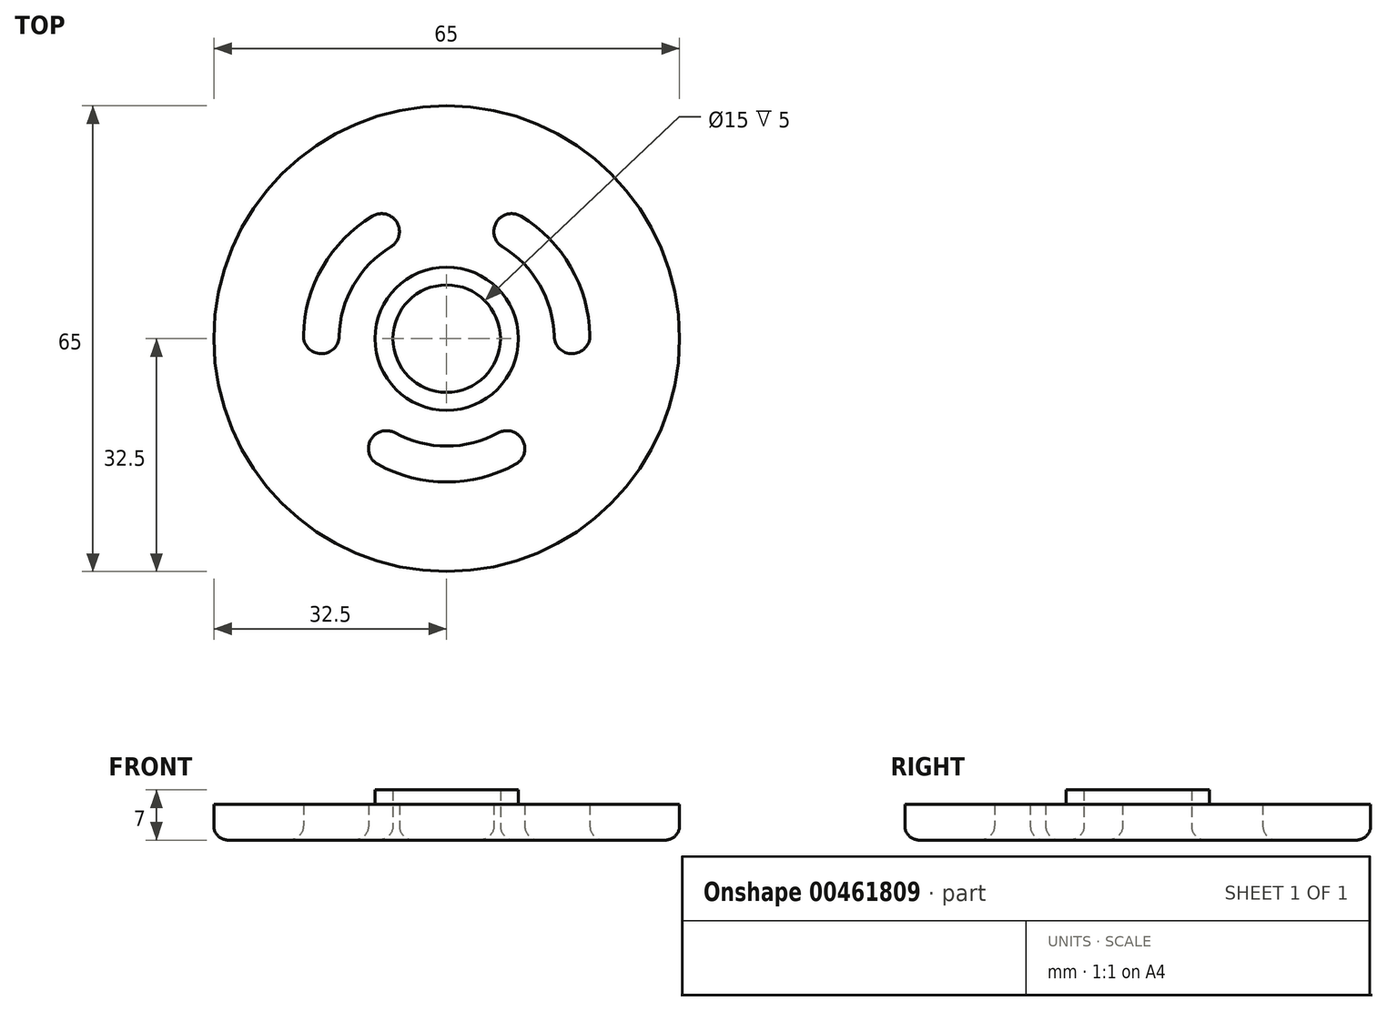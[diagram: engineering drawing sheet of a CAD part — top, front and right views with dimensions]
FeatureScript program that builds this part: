
annotation { "Feature Type Name" : "Feature", "Feature Type Description" : "" }
export const myFeature = defineFeature(function(context is Context, id is Id, definition is map)
    precondition{}
    {
        {
            var Q0;
            Q0=qCreatedBy(makeId("Top.planeOp"),FACE);
            var sketch = newSketch(context, id + "F0", { "sketchPlane" : qUnion([Q0])});
            skCircle(sketch, "E0", {"center": v(0, 0) * mm, "radius": 32.5 * mm});
            skCircle(sketch, "E1", {"center": v(0, 0) * mm, "radius": 10 * mm});
            skLineSegment(sketch, "E2", {"start": v(-10, 0) * mm, "end": v(-15, 0) * mm, "construction": true});
            skCircle(sketch, "E3", {"center": v(0, 0) * mm, "radius": 15 * mm, "construction": true});
            skPoint(sketch, "E4", {"position": v(0, 15) * mm});
            skPoint(sketch, "E5", {"position": v(13, -7.5) * mm});
            skPoint(sketch, "E6", {"position": v(-13, -7.5) * mm});
            skLineSegment(sketch, "E7", {"start": v(0, 0) * mm, "end": v(13, -7.5) * mm});
            skLineSegment(sketch, "E8", {"start": v(0, 15) * mm, "end": v(0, 0) * mm});
            skLineSegment(sketch, "E9", {"start": v(-13, -7.5) * mm, "end": v(0, 0) * mm});
            skLineSegment(sketch, "E10", {"start": v(-9.01, -12) * mm, "end": v(0, 0) * mm, "construction": true});
            skLineSegment(sketch, "E11", {"start": v(0, 0) * mm, "end": v(-14.9, -1.8) * mm, "construction": true});
            skCircle(sketch, "E12", {"center": v(0, 0) * mm, "radius": 20 * mm, "construction": true});
            skLineSegment(sketch, "E13", {"start": v(-17.2, -2.09) * mm, "end": v(-17.2, -2.09) * mm});
            skLineSegment(sketch, "E14", {"start": v(-9.01, -12) * mm, "end": v(-12.02, -15.99) * mm, "construction": true});
            skLineSegment(sketch, "E15", {"start": v(-13, -7.5) * mm, "end": v(-17.32, -10) * mm, "construction": true});
            skLineSegment(sketch, "E16.1.0", {"start": v(14.9, -1.8) * mm, "end": v(19.85, -2.41) * mm, "construction": true});
            skLineSegment(sketch, "E16.1.1", {"start": v(9.01, -12) * mm, "end": v(12.02, -15.99) * mm, "construction": true});
            skLineSegment(sketch, "E16.2.0", {"start": v(-6.79, 15.93) * mm, "end": v(-6.79, 15.93) * mm});
            skLineSegment(sketch, "E16.2.1", {"start": v(5.88, 13.8) * mm, "end": v(7.84, 18.4) * mm, "construction": true});
            skArc(sketch, "E17", {"start": v(-10.39, 17.1) * mm, "mid": v(-17.32, 10) * mm, "end": v(-20, 0.45) * mm});
            skArc(sketch, "E18", {"start": v(-7.79, 12.82) * mm, "mid": v(-13, 7.5) * mm, "end": v(-15, 0.34) * mm});
            skPoint(sketch, "E19.visualSharp", {"position": v(-14.9, -1.8) * mm});
            skArc(sketch, "E19.filletArc", {"start": v(-17.2, -2.09) * mm, "mid": v(-15.64, -1.29) * mm, "end": v(-15, 0.34) * mm});
            skPoint(sketch, "E20.visualSharp", {"position": v(-19.85, -2.41) * mm});
            skArc(sketch, "E20.filletArc", {"start": v(-20, 0.45) * mm, "mid": v(-19.17, -1.46) * mm, "end": v(-17.2, -2.09) * mm});
            skPoint(sketch, "E21.visualSharp", {"position": v(-7.84, 18.4) * mm});
            skArc(sketch, "E21.filletArc", {"start": v(-6.79, 15.93) * mm, "mid": v(-8.32, 17.34) * mm, "end": v(-10.39, 17.1) * mm});
            skPoint(sketch, "E22.visualSharp", {"position": v(-5.88, 13.8) * mm});
            skArc(sketch, "E22.filletArc", {"start": v(-7.79, 12.82) * mm, "mid": v(-6.7, 14.2) * mm, "end": v(-6.79, 15.93) * mm});
            skArc(sketch, "E23.1.0", {"start": v(-10.4, -13.85) * mm, "mid": v(-10.85, -15.88) * mm, "end": v(-9.6, -17.54) * mm});
            skArc(sketch, "E23.1.1", {"start": v(10.4, -13.85) * mm, "mid": v(8.93, -12.9) * mm, "end": v(7.2, -13.16) * mm});
            skArc(sketch, "E23.1.2", {"start": v(-7.2, -13.16) * mm, "mid": v(-8.93, -12.9) * mm, "end": v(-10.4, -13.85) * mm});
            skArc(sketch, "E23.1.3", {"start": v(9.6, -17.54) * mm, "mid": v(10.85, -15.88) * mm, "end": v(10.4, -13.85) * mm});
            skArc(sketch, "E23.2.0", {"start": v(17.2, -2.09) * mm, "mid": v(19.17, -1.46) * mm, "end": v(20, 0.45) * mm});
            skArc(sketch, "E23.2.1", {"start": v(6.79, 15.93) * mm, "mid": v(6.7, 14.2) * mm, "end": v(7.79, 12.82) * mm});
            skArc(sketch, "E23.2.2", {"start": v(15, 0.34) * mm, "mid": v(15.64, -1.29) * mm, "end": v(17.2, -2.09) * mm});
            skArc(sketch, "E23.2.3", {"start": v(10.39, 17.1) * mm, "mid": v(8.32, 17.34) * mm, "end": v(6.79, 15.93) * mm});
            skArc(sketch, "E24.1.0", {"start": v(-7.2, -13.16) * mm, "mid": v(0, -15) * mm, "end": v(7.2, -13.16) * mm});
            skArc(sketch, "E24.2.0", {"start": v(15, 0.34) * mm, "mid": v(13, 7.5) * mm, "end": v(7.79, 12.82) * mm});
            skArc(sketch, "E25.1.0", {"start": v(-9.6, -17.54) * mm, "mid": v(0, -20) * mm, "end": v(9.6, -17.54) * mm});
            skArc(sketch, "E25.2.0", {"start": v(20, 0.45) * mm, "mid": v(17.32, 10) * mm, "end": v(10.39, 17.1) * mm});
            skSolve(sketch);
        }
        {
            var Q0;
            Q0=makeQuery(id+"F0.imprint","IMPRINT",FACE,{"disambiguationData":[TD([[makeQuery(id+"F0.imprint","IMPRINT",EDGE,{"derivedFrom":sQuery(id+"F0.wireOp",EDGE,"E0")}),1.0]])]});
            extrude(context, id + "F1", {"entities" : qUnion([Q0]), "depth" : 5 * mm});
        }
        {
            var Q0;
            Q0=makeQuery(id+"F1.opExtrude","CAP_FACE",FACE,{"disambiguationData":[OSD([sQuery(id+"F0.wireOp",EDGE,"E0"),sQuery(id+"F0.wireOp",EDGE,"E1"),sQuery(id+"F0.wireOp",EDGE,"E17"),sQuery(id+"F0.wireOp",EDGE,"E18"),sQuery(id+"F0.wireOp",EDGE,"E19.filletArc"),sQuery(id+"F0.wireOp",EDGE,"E20.filletArc"),sQuery(id+"F0.wireOp",EDGE,"E21.filletArc"),sQuery(id+"F0.wireOp",EDGE,"E22.filletArc"),sQuery(id+"F0.wireOp",EDGE,"E23.1.0"),sQuery(id+"F0.wireOp",EDGE,"E23.1.1"),sQuery(id+"F0.wireOp",EDGE,"E23.1.2"),sQuery(id+"F0.wireOp",EDGE,"E23.1.3"),sQuery(id+"F0.wireOp",EDGE,"E23.2.0"),sQuery(id+"F0.wireOp",EDGE,"E23.2.1"),sQuery(id+"F0.wireOp",EDGE,"E23.2.2"),sQuery(id+"F0.wireOp",EDGE,"E23.2.3"),sQuery(id+"F0.wireOp",EDGE,"E24.1.0"),sQuery(id+"F0.wireOp",EDGE,"E24.2.0"),sQuery(id+"F0.wireOp",EDGE,"E25.1.0"),sQuery(id+"F0.wireOp",EDGE,"E25.2.0")])],"isStart":true});
            var sketch = newSketch(context, id + "F2", { "sketchPlane" : qUnion([Q0])});
            skCircle(sketch, "E26.0", {"center": v(0, 0) * mm, "radius": 10 * mm});
            skCircle(sketch, "E27.0", {"center": v(0, 0) * mm, "radius": 7.5 * mm});
            skSolve(sketch);
        }
        {
            var Q0;
            Q0=makeQuery(id+"F2.imprint","IMPRINT",FACE,{"disambiguationData":[TD([[makeQuery(id+"F2.imprint","IMPRINT",EDGE,{"derivedFrom":sQuery(id+"F2.wireOp",EDGE,"E26.0")}),-1.0]])]});
            extrude(context, id + "F3", {"entities" : qUnion([Q0]), "operationType" : NewBodyOperationType.ADD, "oppositeDirection" : true, "depth" : 7 * mm});
        }
        {
            var Q0;
            Q0=makeQuery(id+"F3.boolean.opBoolean","MERGE",FACE,{"derivedFrom":[makeQuery(id+"F1.opExtrude","CAP_FACE",FACE,{"disambiguationData":[OSD([sQuery(id+"F0.wireOp",EDGE,"E0"),sQuery(id+"F0.wireOp",EDGE,"E1"),sQuery(id+"F0.wireOp",EDGE,"E17"),sQuery(id+"F0.wireOp",EDGE,"E18"),sQuery(id+"F0.wireOp",EDGE,"E19.filletArc"),sQuery(id+"F0.wireOp",EDGE,"E20.filletArc"),sQuery(id+"F0.wireOp",EDGE,"E21.filletArc"),sQuery(id+"F0.wireOp",EDGE,"E22.filletArc"),sQuery(id+"F0.wireOp",EDGE,"E23.1.0"),sQuery(id+"F0.wireOp",EDGE,"E23.1.1"),sQuery(id+"F0.wireOp",EDGE,"E23.1.2"),sQuery(id+"F0.wireOp",EDGE,"E23.1.3"),sQuery(id+"F0.wireOp",EDGE,"E23.2.0"),sQuery(id+"F0.wireOp",EDGE,"E23.2.1"),sQuery(id+"F0.wireOp",EDGE,"E23.2.2"),sQuery(id+"F0.wireOp",EDGE,"E23.2.3"),sQuery(id+"F0.wireOp",EDGE,"E24.1.0"),sQuery(id+"F0.wireOp",EDGE,"E24.2.0"),sQuery(id+"F0.wireOp",EDGE,"E25.1.0"),sQuery(id+"F0.wireOp",EDGE,"E25.2.0")])],"isStart":true}),makeQuery(id+"F3.opExtrude","CAP_FACE",FACE,{"disambiguationData":[OSD([sQuery(id+"F2.wireOp",EDGE,"E26.0"),sQuery(id+"F2.wireOp",EDGE,"E27.0")])],"isStart":true})]});
            fillet(context, id + "F4", {"entities" : qUnion([Q0]), "radius" : 2 * mm, "tangentPropagation" : true, "allowEdgeOverflow" : false});
        }
    });
